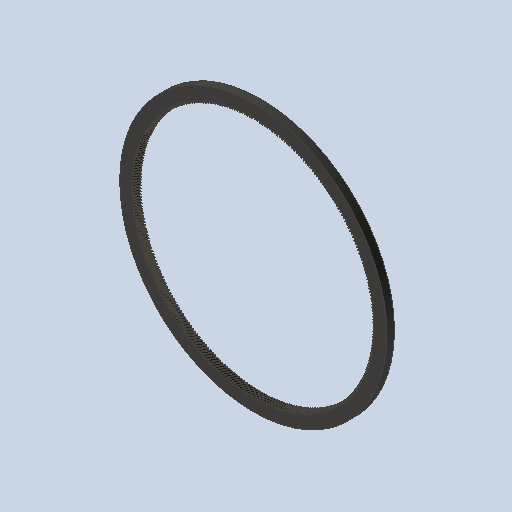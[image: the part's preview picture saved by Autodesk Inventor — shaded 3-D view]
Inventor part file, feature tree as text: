
AUTODESK INVENTOR PART (.ipt)
format: ipt  version: 2023 (Build 270158000, 158)  size: 3,260,928 bytes
history: native  units: mm (DEFAULTED — no unit token found)
features: plane x3, other x3, sketch x2, extrude x1
ambient origin geometry x8: Origin, YZ Plane, XZ Plane, XY Plane, X Axis, Y Axis, Z Axis, Center Point
bodies: Solid1 (feature_tree)
feature tree (9):
  extrude  "Extrusion1"  Depth=10.0mm TaperAngle=0.0deg
  plane  "Work Plane2"
  plane  "Work Plane8"
  plane  "Work Plane9"
  other  "Spur Gear"
  sketch  "Sketch1"  dims[d0=354.34251mm d1=10.0mm d2=0.0mm]
  sketch  "Sketch2"  dims[d3=319.253332mm d4=10.0mm d5=0.0mm d16=80.0mm d17=0.0mm d34=0.10472mm d39=0.0mm d45=0.0mm d47=80.0mm d50=0.0mm d51=0.0mm d52=80.0mm]
  other  "Srf1"
  other  "Pitch Diameter"
